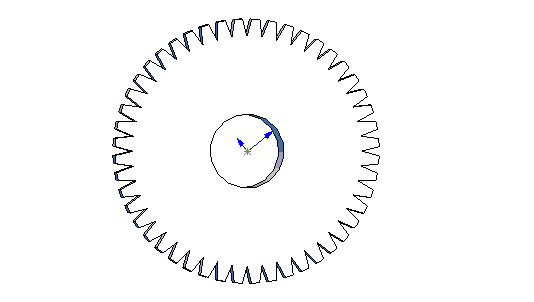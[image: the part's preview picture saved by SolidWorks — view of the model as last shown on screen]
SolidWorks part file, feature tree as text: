
SOLIDWORKS PART (.sldprt)
format: sldprt  version: not decoded by parser v0  size: 385,536 bytes
history: native  units: mm
features: sketch x4, extrude x2, cut_extrude x2 (+11 scaffold rows collapsed)
feature tree (19):
  scaffold x11  (default folders/planes/origin — collapsed)
  sketch  "Sketch1"  dims[D1=11.303mm]
  extrude  "Extrude1"  Depth=3.175mm
  sketch  "Sketch2"  dims[D1=9.0932mm]
  extrude  "Extrude2"  Depth=4.572mm
  sketch  "Sketch3"  dims[D1=3.175mm]
  cut_extrude  "Cut-Extrude1"  [1 undecoded]
  sketch  "Sketch7"  dims[D1=9.8044mm]
  cut_extrude  "Cut-Extrude5"  Depth=4.572mm
decode coverage: 7 of 8 modeling features carry decoded parameters
note: 1 parameter value undecoded
note: suppression state not decoded; provenance and decode notes live in map.json
